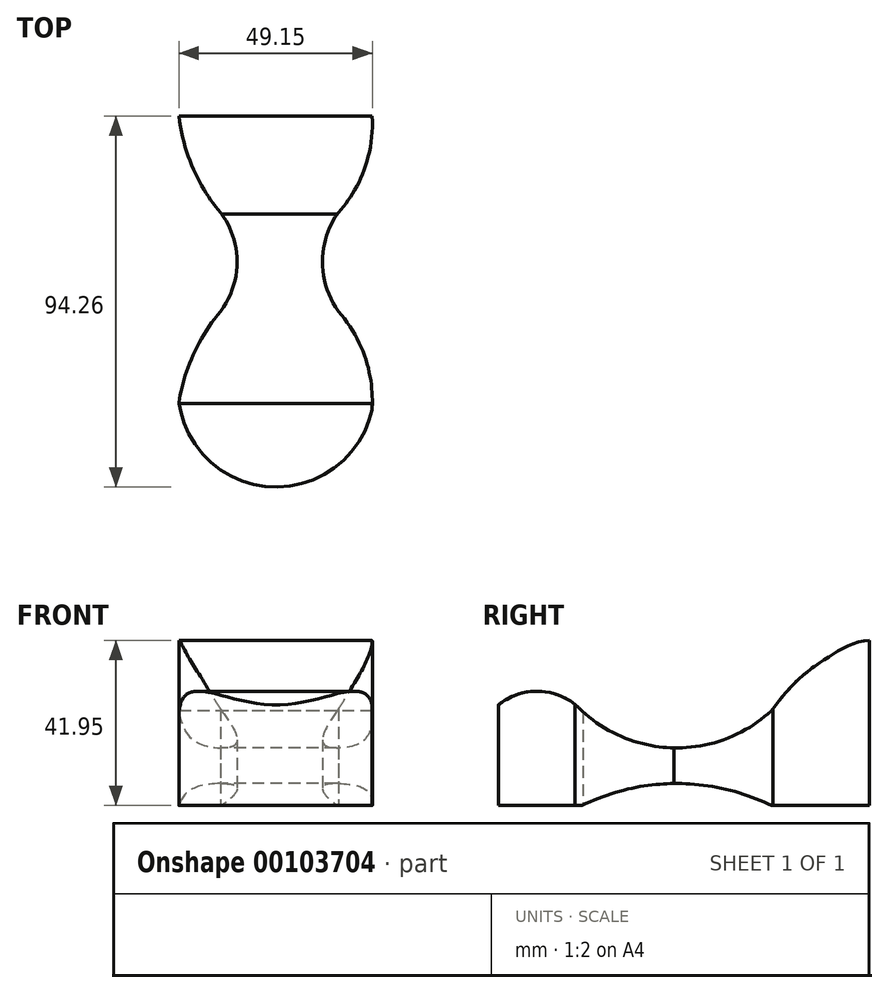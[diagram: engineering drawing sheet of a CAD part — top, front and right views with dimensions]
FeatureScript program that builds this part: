
annotation { "Feature Type Name" : "Feature", "Feature Type Description" : "" }
export const myFeature = defineFeature(function(context is Context, id is Id, definition is map)
    precondition{}
    {
        {
            var Q0;
            Q0=qCreatedBy(makeId("Top.planeOp"),FACE);
            var sketch = newSketch(context, id + "F0", { "sketchPlane" : qUnion([Q0])});
            skArc(sketch, "E0", {"start": v(-25.75, -23.12) * mm, "mid": v(-2.05, -44.61) * mm, "end": v(23.32, -25.12) * mm});
            skArc(sketch, "E1", {"start": v(-15.2, 0) * mm, "mid": v(-22, -10.86) * mm, "end": v(-25.75, -23.12) * mm});
            skArc(sketch, "E2", {"start": v(-15.2, 0) * mm, "mid": v(-10.96, 12.55) * mm, "end": v(-15.2, 25.1) * mm});
            skArc(sketch, "E3", {"start": v(-25.75, 49.63) * mm, "mid": v(-22.28, 36.58) * mm, "end": v(-15.2, 25.1) * mm});
            skArc(sketch, "E4", {"start": v(23.32, -25.12) * mm, "mid": v(21.56, -11.7) * mm, "end": v(14.76, 0) * mm});
            skArc(sketch, "E5", {"start": v(14.76, 25.1) * mm, "mid": v(10.74, 12.55) * mm, "end": v(14.76, 0) * mm});
            skArc(sketch, "E6", {"start": v(14.76, 25.1) * mm, "mid": v(21.52, 36.5) * mm, "end": v(23.32, 49.63) * mm});
            skLineSegment(sketch, "E7", {"start": v(-25.75, 49.63) * mm, "end": v(23.32, 49.63) * mm});
            skSolve(sketch);
        }
        {
            var Q0;
            Q0 = qSketchRegion(id + "F0", true);
            extrude(context, id + "F1", {"entities" : qUnion([Q0]), "depth" : 50.8 * mm});
        }
        {
            var Q0;
            Q0=qCreatedBy(makeId("Right.planeOp"),FACE);
            var sketch = newSketch(context, id + "F2", { "sketchPlane" : qUnion([Q0])});
            skArc(sketch, "E8", {"start": v(-23.42, 24.08) * mm, "mid": v(0.66, 14.66) * mm, "end": v(24.74, 24.08) * mm});
            skArc(sketch, "E9", {"start": v(24.74, 0) * mm, "mid": v(0.66, 5.6) * mm, "end": v(-23.42, 0) * mm});
            skLineSegment(sketch, "E10", {"start": v(-23.42, 0) * mm, "end": v(24.74, 0) * mm});
            skFitSpline(sketch, "E11", {"points": [v(24.74, 24.08) * mm, v(32.8, 33.07) * mm, v(46.22, 41.37) * mm, v(50.2, 41.94) * mm], "startDerivative": vector(18.23, 24.21) * mm, "endDerivative": vector(15.85, -0.23) * mm});
            skLineSegment(sketch, "E12", {"start": v(50.2, 41.94) * mm, "end": v(50.2, 52.8) * mm});
            skLineSegment(sketch, "E13", {"start": v(50.2, 52.8) * mm, "end": v(50.2, 41.94) * mm});
            skLineSegment(sketch, "E14", {"start": v(50.2, 0) * mm, "end": v(24.74, 0) * mm});
            skLineSegment(sketch, "E15", {"start": v(50.2, 0) * mm, "end": v(50.2, 41.94) * mm});
            skArc(sketch, "E16", {"start": v(-23.42, 24.08) * mm, "mid": v(-34.81, 29.04) * mm, "end": v(-46.2, 24.08) * mm});
            skLineSegment(sketch, "E17", {"start": v(-23.42, 0) * mm, "end": v(-46.2, 0) * mm});
            skLineSegment(sketch, "E18", {"start": v(-46.2, 0) * mm, "end": v(-46.2, 24.08) * mm});
            skLineSegment(sketch, "E19", {"start": v(-46.2, 24.08) * mm, "end": v(-46.2, 52.8) * mm});
            skLineSegment(sketch, "E20", {"start": v(-46.2, 52.8) * mm, "end": v(50.2, 52.8) * mm});
            skSolve(sketch);
        }
        {
            var Q0;
            Q0=makeQuery(id+"F2.imprint","IMPRINT",FACE,{"disambiguationData":[TD([[makeQuery(id+"F2.imprint","IMPRINT",EDGE,{"derivedFrom":sQuery(id+"F2.wireOp",EDGE,"E9")}),1.0]])]});
            var Q1;
            Q1=makeQuery(id+"F2.imprint","IMPRINT",FACE,{"disambiguationData":[TD([[makeQuery(id+"F2.imprint","IMPRINT",EDGE,{"derivedFrom":sQuery(id+"F2.wireOp",EDGE,"E8")}),1.0]])]});
            extrude(context, id + "F3", {"entities" : qUnion([Q0, Q1]), "operationType" : NewBodyOperationType.REMOVE, "depth" : 25.4 * mm});
        }
        {
            var Q0;
            Q0=makeQuery(id+"F2.imprint","IMPRINT",FACE,{"disambiguationData":[TD([[makeQuery(id+"F2.imprint","IMPRINT",EDGE,{"derivedFrom":sQuery(id+"F2.wireOp",EDGE,"E8")}),1.0]])]});
            var Q1;
            Q1=makeQuery(id+"F2.imprint","IMPRINT",FACE,{"disambiguationData":[TD([[makeQuery(id+"F2.imprint","IMPRINT",EDGE,{"derivedFrom":sQuery(id+"F2.wireOp",EDGE,"E9")}),1.0]])]});
            extrude(context, id + "F4", {"entities" : qUnion([Q0, Q1]), "operationType" : NewBodyOperationType.REMOVE, "oppositeDirection" : true, "depth" : 50.8 * mm});
        }
    });
